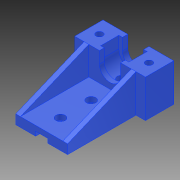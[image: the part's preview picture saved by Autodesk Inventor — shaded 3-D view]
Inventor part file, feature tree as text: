
AUTODESK INVENTOR PART (.ipt)
format: ipt  version: 2015 (Build 190159000, 159)  size: 161,280 bytes
history: native  units: in
note: dims shown in document units (in); Inventor stores cm internally (conversion verified against a paired STEP export)
features: other x7, direct_edit x3, sketch x1, imported_body x1
ambient origin geometry x8: Origin, YZ Plane, XZ Plane, XY Plane, X Axis, Y Axis, Z Axis, Center Point
bodies: Body1 (feature_tree)
feature tree (12):
  other  "Boss-Extrude4"
  other  "luerholder.ipt1"
  direct_edit  "Direct Edit1"
  sketch  "Sketch1"  dims[d2=1.1811in d3=0.0709in]
  direct_edit  "Direct Edit2"
  direct_edit  "Direct Edit3"
  imported_body  "Base1"
  other  "Delete1"
  other  "Delete2"
  other  "Delete3"
  other  "Size1"
  other  "Size2"
